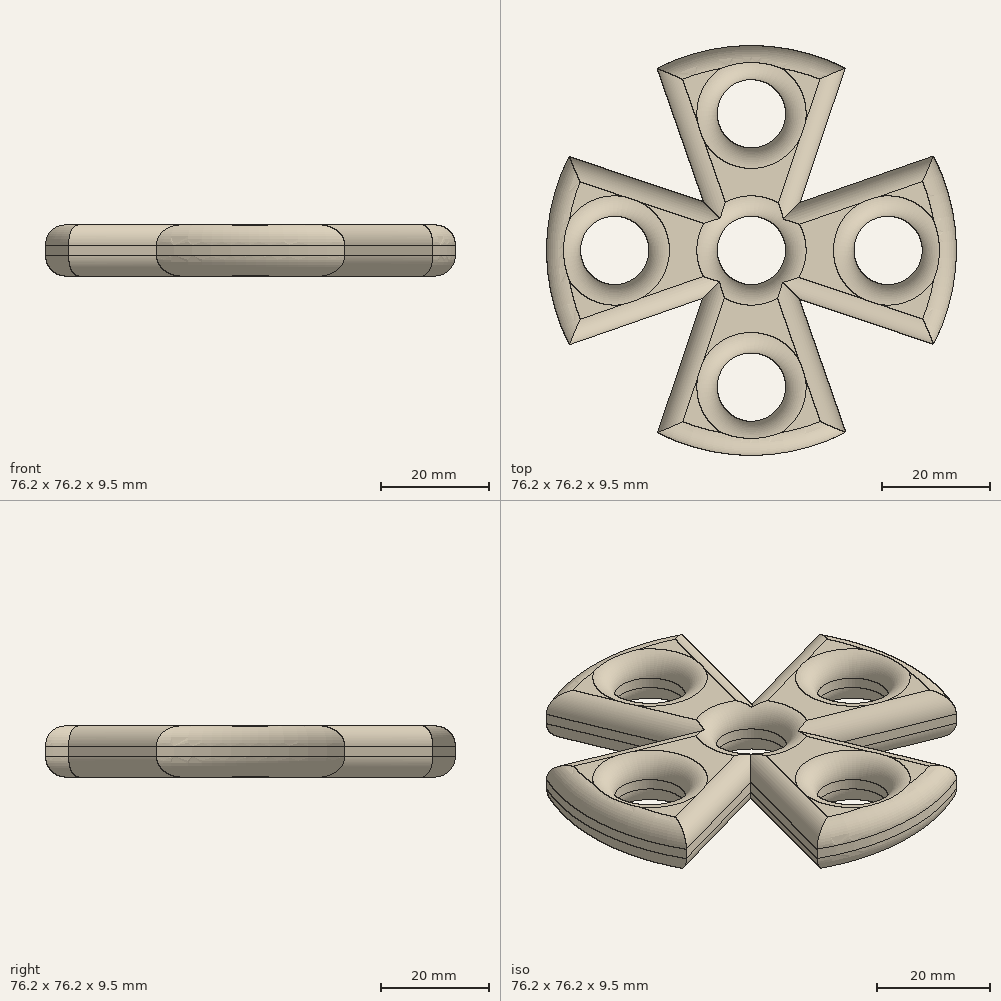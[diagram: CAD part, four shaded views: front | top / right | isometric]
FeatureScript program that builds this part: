
annotation { "Feature Type Name" : "Feature", "Feature Type Description" : "" }
export const myFeature = defineFeature(function(context is Context, id is Id, definition is map)
    precondition{}
    {
        {
            var Q0;
            Q0=qCreatedBy(makeId("Top.planeOp"),FACE);
            var sketch = newSketch(context, id + "F0", { "sketchPlane" : qUnion([Q0])});
            skCircle(sketch, "E0", {"center": v(0, 0) * mm, "radius": 38.1 * mm});
            skSolve(sketch);
        }
        {
            var Q0;
            Q0=qSketchRegion(id+"F0",true);
            extrude(context, id + "F1", {"entities" : qUnion([Q0]), "depth" : 9.52 * mm, "offsetDistance" : 25.4 * mm});
        }
        {
            var Q0;
            Q0=qCreatedBy(makeId("Top.planeOp"),FACE);
            var sketch = newSketch(context, id + "F2", { "sketchPlane" : qUnion([Q0])});
            skCircle(sketch, "E1", {"center": v(0, 0) * mm, "radius": 6.35 * mm});
            skSolve(sketch);
        }
        {
            var Q0;
            Q0=qSketchRegion(id+"F2",true);
            extrude(context, id + "F3", {"entities" : qUnion([Q0]), "operationType" : NewBodyOperationType.REMOVE, "depth" : 25.4 * mm, "offsetDistance" : 25.4 * mm});
        }
        {
            var Q0;
            Q0=qCreatedBy(makeId("Top.planeOp"),FACE);
            var sketch = newSketch(context, id + "F4", { "sketchPlane" : qUnion([Q0])});
            skCircle(sketch, "E2", {"center": v(0, 0) * mm, "radius": 12.7 * mm, "construction": true});
            skCircle(sketch, "E3", {"center": v(-25.4, 0) * mm, "radius": 6.35 * mm});
            skCircle(sketch, "E4.1.0", {"center": v(0, -25.4) * mm, "radius": 6.35 * mm});
            skCircle(sketch, "E4.2.0", {"center": v(25.4, 0) * mm, "radius": 6.35 * mm});
            skCircle(sketch, "E4.3.0", {"center": v(0, 25.4) * mm, "radius": 6.35 * mm});
            skLineSegment(sketch, "E5", {"start": v(-44.75, 21.1) * mm, "end": v(-8.91, 9.05) * mm});
            skLineSegment(sketch, "E6", {"start": v(-8.91, 9.05) * mm, "end": v(-17.77, 34.46) * mm});
            skLineSegment(sketch, "E7", {"start": v(-44.75, 21.1) * mm, "end": v(-17.77, 34.46) * mm});
            skLineSegment(sketch, "E8.1.0", {"start": v(-21.1, -44.75) * mm, "end": v(-34.46, -17.77) * mm});
            skLineSegment(sketch, "E8.1.1", {"start": v(-9.05, -8.91) * mm, "end": v(-34.46, -17.77) * mm});
            skLineSegment(sketch, "E8.1.2", {"start": v(-21.1, -44.75) * mm, "end": v(-9.05, -8.91) * mm});
            skLineSegment(sketch, "E8.2.0", {"start": v(44.75, -21.1) * mm, "end": v(17.77, -34.46) * mm});
            skLineSegment(sketch, "E8.2.1", {"start": v(8.91, -9.05) * mm, "end": v(17.77, -34.46) * mm});
            skLineSegment(sketch, "E8.2.2", {"start": v(44.75, -21.1) * mm, "end": v(8.91, -9.05) * mm});
            skLineSegment(sketch, "E8.3.0", {"start": v(21.1, 44.75) * mm, "end": v(34.46, 17.77) * mm});
            skLineSegment(sketch, "E8.3.1", {"start": v(9.05, 8.91) * mm, "end": v(34.46, 17.77) * mm});
            skLineSegment(sketch, "E8.3.2", {"start": v(21.1, 44.75) * mm, "end": v(9.05, 8.91) * mm});
            skSolve(sketch);
        }
        {
            var Q0;
            Q0=qSketchRegion(id+"F4",true);
            extrude(context, id + "F5", {"entities" : qUnion([Q0]), "operationType" : NewBodyOperationType.REMOVE, "depth" : 25.4 * mm, "offsetDistance" : 25.4 * mm});
        }
        {
            var Q0;
            Q0=makeQuery(id+"F1.opExtrude","CAP_FACE",FACE,{"disambiguationData":[OSD([sQuery(id+"F0.wireOp",EDGE,"E0")])],"isStart":true});
            var Q1;
            Q1=makeQuery(id+"F1.opExtrude","CAP_FACE",FACE,{"disambiguationData":[OSD([sQuery(id+"F0.wireOp",EDGE,"E0")])],"isStart":false});
            fillet(context, id + "F6", {"entities" : qUnion([Q0, Q1]), "radius" : 3.8 * mm, "tangentPropagation" : true, "allowEdgeOverflow" : false});
        }
    });
